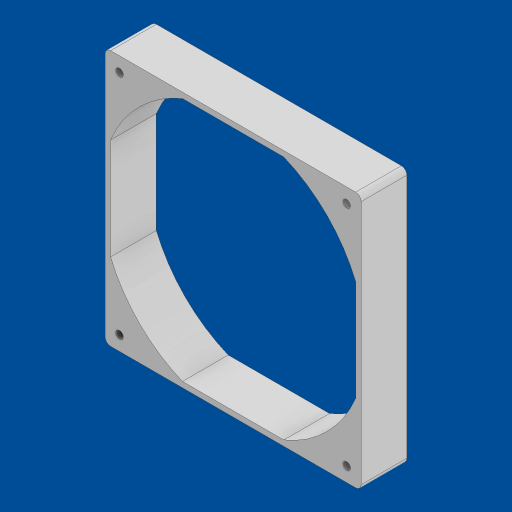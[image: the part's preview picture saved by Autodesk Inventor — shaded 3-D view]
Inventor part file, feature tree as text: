
AUTODESK INVENTOR PART (.ipt)
format: ipt  version: 2023.2 (Build 272271000, 271)  size: 129,536 bytes
history: native  units: mm
features: sketch x1, extrude x1, hole x1
ambient origin geometry x8: Origin, YZ Plane, XZ Plane, XY Plane, X Axis, Y Axis, Z Axis, Center Point
bodies: Solid1 (feature_tree)
feature tree (3):
  sketch  "Sketch1"  dims[d0=140.0mm d1=140.0mm d2=3.0mm d3=124.2mm d4=124.2mm d5=145.0mm d6=145.0mm d7=134.0mm d8=25.0mm d9=0.0mm d10=4.134mm d11=10.0mm d12=4.0mm d13=2.0mm d14=90.0deg d15=8.0mm d16=20.594885mm]
  extrude  "Extrusion1"  Depth=140.0mm
  hole  "Hole1"  [1 undecoded]
note: 1 required parameter value undecoded (feature->parameter linkage not recoverable at this tier; creation-order binding heuristic only, values carry confidence <= 0.55)
